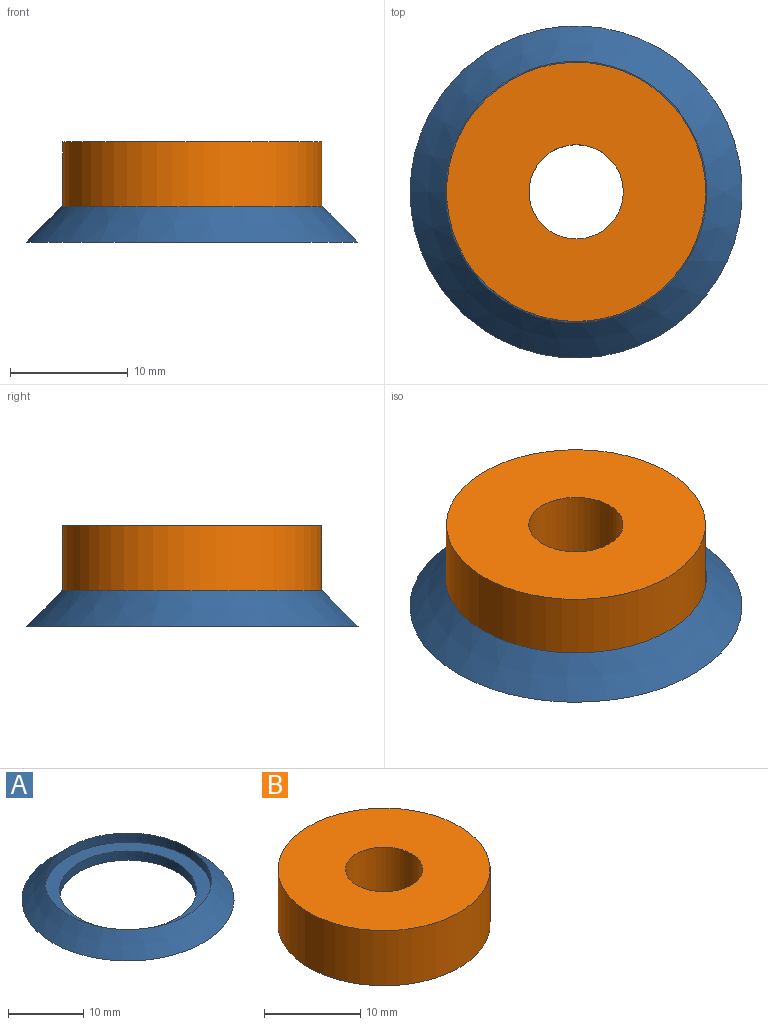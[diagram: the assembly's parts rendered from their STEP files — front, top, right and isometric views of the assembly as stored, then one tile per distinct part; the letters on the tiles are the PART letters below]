
ASSEMBLY  parts=2 mates=1
PART A: 5 faces, bbox 28.2x28.2x3 mm
  f0: cone r=11.1mm half-angle=45deg, axis (0,0,-1), area 335.9mm2, adj f1,f4
  f1: cylinder r=11.1mm len=22.2mm, axis (0,0,-1), area 104.6mm2, adj f0,f2
  f2: plane 22.2x22.2mm, normal (0,0,1), area 126.9mm2, adj f1,f3
  f3: cylinder r=9.1mm len=18.2mm, axis (0,0,-1), area 85.8mm2, adj f2,f4
  f4: plane 28.2x28.2mm, normal (0,0,-1), area 364.4mm2, adj f0,f3
PART B: 4 faces, bbox 22x22x7 mm
  f0: cylinder r=4mm len=8mm, axis (0,0,-1), area 175.9mm2, adj f2,f3
  f1: cylinder r=11mm len=22mm, axis (0,0,-1), area 483.8mm2, adj f2,f3
  f2: plane 22x22mm, normal (0,0,1), area 329.9mm2, adj f0,f1
  f3: plane 22x22mm, normal (0,0,-1), area 329.9mm2, adj f0,f1
PLACE A t=(4.74,5.32,0.07)mm
PLACE B rot(axis=(1,0,0),180deg) t=(4.74,5.32,2.27)mm
MATE fastened B.f0 <-> A.f0  axis (0,0,1) through (4.74,5.32,-4.73)mm
